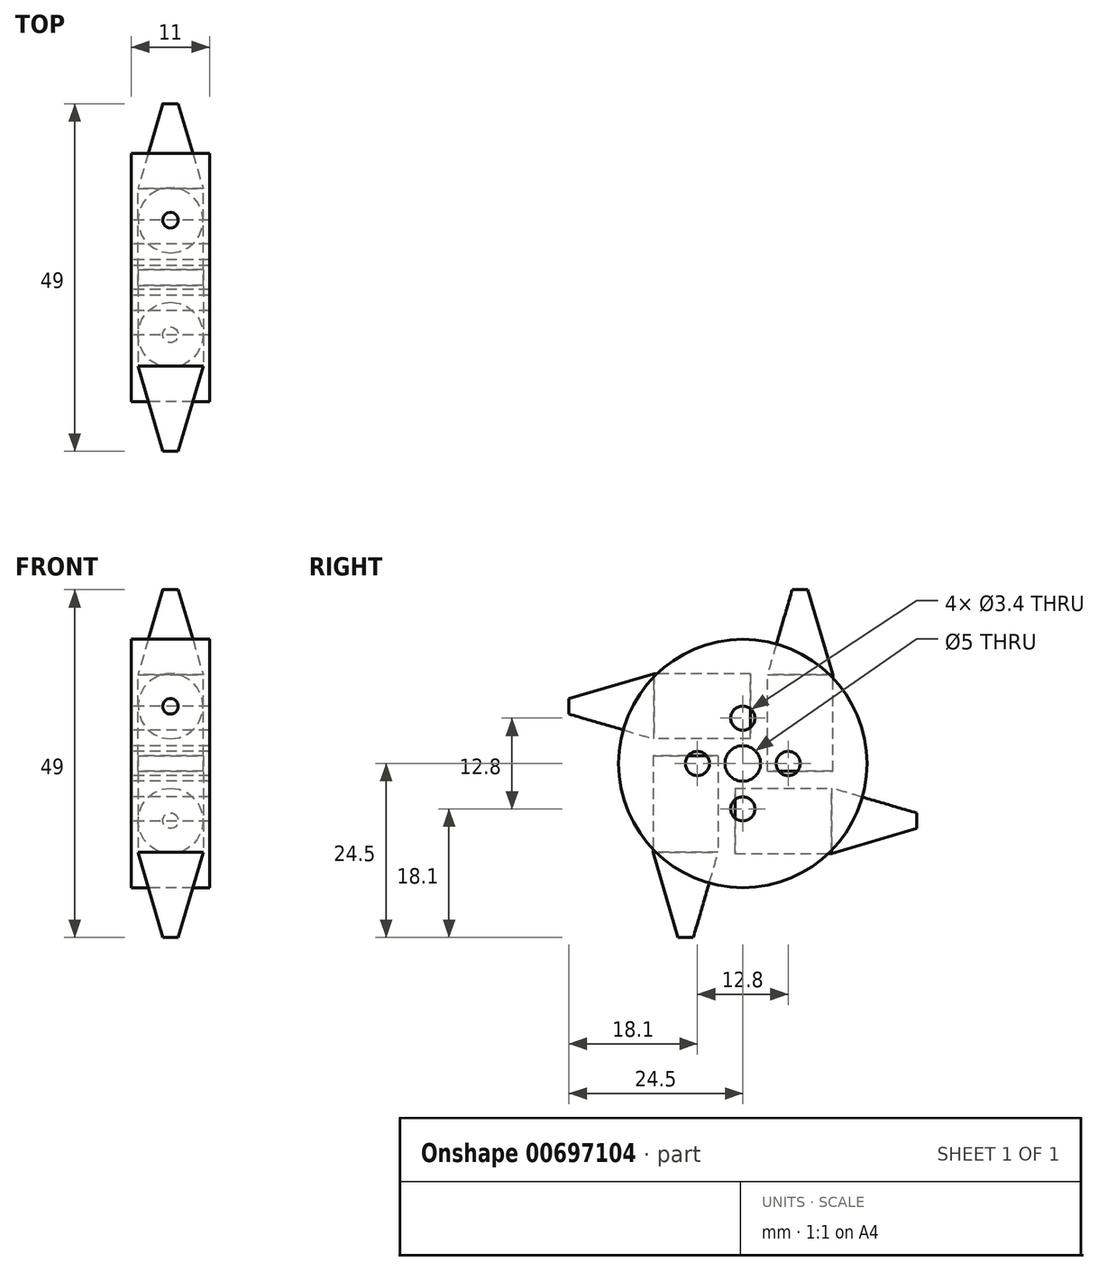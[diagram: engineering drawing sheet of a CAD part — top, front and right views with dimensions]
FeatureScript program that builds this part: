
annotation { "Feature Type Name" : "Feature", "Feature Type Description" : "" }
export const myFeature = defineFeature(function(context is Context, id is Id, definition is map)
    precondition{}
    {
        {
            var Q0;
            Q0=qCreatedBy(makeId("Right.planeOp"),FACE);
            var sketch = newSketch(context, id + "F0", { "sketchPlane" : qUnion([Q0])});
            skCircle(sketch, "E0", {"center": v(0, 0) * mm, "radius": 17.5 * mm});
            skCircle(sketch, "E1", {"center": v(0, 0) * mm, "radius": 2.5 * mm});
            skCircle(sketch, "E2", {"center": v(0, 6.4) * mm, "radius": 1.7 * mm});
            skCircle(sketch, "E3", {"center": v(6.4, 0) * mm, "radius": 1.7 * mm});
            skCircle(sketch, "E4", {"center": v(0, -6.4) * mm, "radius": 1.7 * mm});
            skCircle(sketch, "E5", {"center": v(-6.4, 0) * mm, "radius": 1.7 * mm});
            skSolve(sketch);
        }
        {
            var Q0;
            Q0=qSketchRegion(id+"F0",true);
            extrude(context, id + "F1", {"entities" : qUnion([Q0]), "endBound" : BoundingType.SYMMETRIC, "depth" : 11 * mm, "offsetDistance" : 25 * mm});
        }
        {
            var Q0;
            Q0=qCreatedBy(makeId("Top.planeOp"),FACE);
            var sketch = newSketch(context, id + "F2", { "sketchPlane" : qUnion([Q0])});
            skLineSegment(sketch, "E6", {"start": v(-19.71, 0) * mm, "end": v(30.41, 0) * mm});
            skSolve(sketch);
        }
        {
            var Q0;
            Q0=qCreatedBy(makeId("Right.planeOp"),FACE);
            var sketch = newSketch(context, id + "F3", { "sketchPlane" : qUnion([Q0])});
            skLineSegment(sketch, "E7.top", {"start": v(1.1, 8.07) * mm, "end": v(1.1, 3.47) * mm});
            skLineSegment(sketch, "E7.left", {"start": v(-12.5, 8.07) * mm, "end": v(1.1, 8.07) * mm});
            skLineSegment(sketch, "E7.right", {"start": v(-12.5, 3.47) * mm, "end": v(1.1, 3.47) * mm});
            skLineSegment(sketch, "E8", {"start": v(-12.5, 3.47) * mm, "end": v(-24.5, 6.97) * mm});
            skLineSegment(sketch, "E9", {"start": v(-24.5, 6.97) * mm, "end": v(-24.5, 8.07) * mm});
            skLineSegment(sketch, "E10", {"start": v(-24.5, 8.07) * mm, "end": v(-12.5, 8.07) * mm});
            skSolve(sketch);
        }
        {
            var Q0;
            Q0=makeQuery(id+"F3.imprint","IMPRINT",FACE,{"disambiguationData":[TD([[makeQuery(id+"F3.imprint","IMPRINT",EDGE,{"derivedFrom":sQuery(id+"F3.wireOp",EDGE,"E7.top")}),-1.0]])]});
            var Q1;
            Q1=sQuery(id+"F3.wireOp",EDGE,"E10");
            revolve(context, id + "F4", {"entities" : qUnion([Q0]), "axis" : qUnion([Q1]), "revolveType" : RevolveType.FULL});
        }
        {
            var Q0;
            Q0=makeQuery(id+"F4.opRevolve","SWEPT_BODY",BODY,{"disambiguationData":[OSD([sQuery(id+"F3.wireOp",EDGE,"E7.top"),sQuery(id+"F3.wireOp",EDGE,"E7.left"),sQuery(id+"F3.wireOp",EDGE,"E7.right"),sQuery(id+"F3.wireOp",EDGE,"E8"),sQuery(id+"F3.wireOp",EDGE,"E9"),sQuery(id+"F3.wireOp",EDGE,"E10")])]});
            var Q1;
            Q1=sQuery(id+"F2.wireOp",EDGE,"E6");
            circularPattern(context, id + "F5", {"entities" : qUnion([Q0]), "axis" : qUnion([Q1]), "angle" : 360 * degree, "instanceCount" : 4, "equalSpace" : true});
        }
    });
